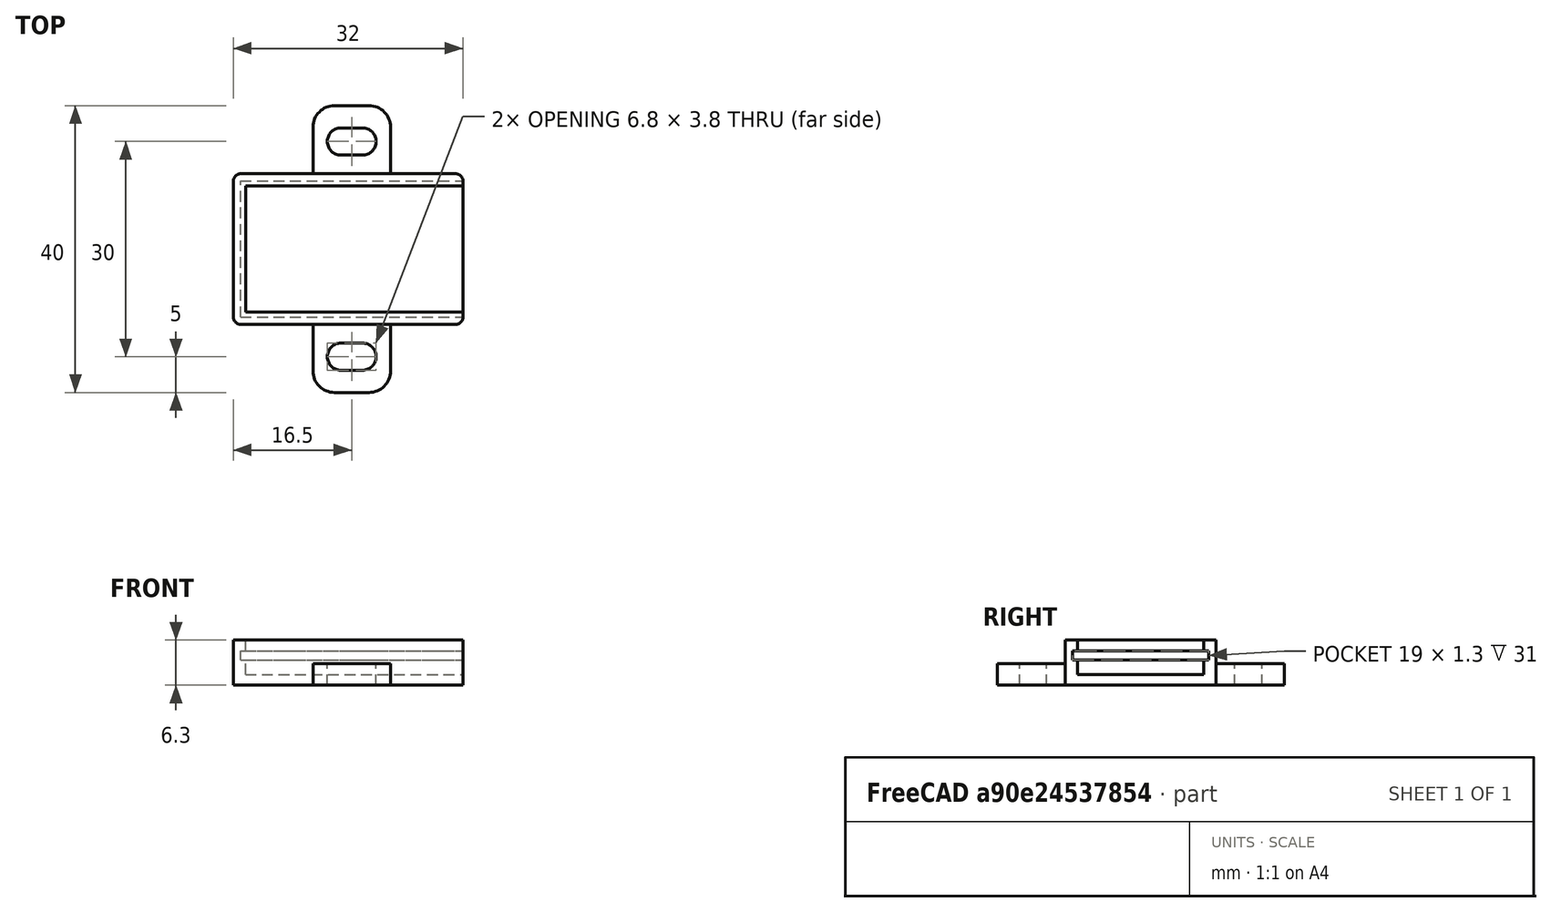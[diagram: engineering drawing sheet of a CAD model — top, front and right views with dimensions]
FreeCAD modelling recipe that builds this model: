
FCSTD DOCUMENT  (FreeCAD 0.18.4R)
Label: stm8s003f
License: FreeArt
LicenseURL: http://artlibre.org/licence/lal
objects: Part::Box×3, Part::MultiFuse×2, Spreadsheet::Sheet×1, Part::Fillet×1, Part::Feature×1, Part::Cut×1, App::Part×1
note: 8 computed .brp shape members not serialized (recipe doc carries the construction recipe); baked Part::Feature solids carry a one-line shape summary decoded from their .brp

FEATURE [Spreadsheet::Sheet] Spreadsheet  label="p"
  cells = A1=pcb_x; B1(pcb_x)=31; A2=pcb_y; B2(pcb_y)=19; A3=pcb_z; B3(pcb_z)=1.3; A4=pcb_under; B4(pcb_under)=2; A5=side_wall; B5(side_wall)=1; A6=pcb_side_lane; B6(pcb_side_lane)=0.7; A7=bottom_wall; B7(bottom_wall)=1.5; A8=pcb_above; B8(pcb_above)=1.5
FEATURE [Part::Box] Box  label="external cube"
  AttacherType = Attacher::AttachEngine3D
  Height = 6.3
  Length = 32
  Width = 21
  expr: Height = p.bottom_wall + p.pcb_under + p.pcb_z + p.pcb_above
  expr: Width = p.pcb_y + 2 * p.side_wall
  expr: Length = p.pcb_x + p.side_wall
FEATURE [Part::Box] Box006  label="internal cube"
  AttacherType = Attacher::AttachEngine3D
  Height = 4.8
  Length = 30.6
  Placement = pos=(1.7,1.7,1.5) rot=(0,0,1;0rad)
  Width = 17.6
  expr: Placement.Base.y = p.side_wall + p.pcb_side_lane
  expr: Placement.Base.x = p.side_wall + p.pcb_side_lane
  expr: Placement.Base.z = p.bottom_wall
  expr: Height = p.pcb_under + p.pcb_z + p.pcb_above
  expr: Width = p.pcb_y - 2 * p.pcb_side_lane
  expr: Length = p.pcb_x - 2 * p.pcb_side_lane + p.side_wall
FEATURE [Part::Box] Box007  label="pcb extract cube"
  AttacherType = Attacher::AttachEngine3D
  Height = 1.3
  Length = 31
  Placement = pos=(1,1,3.5) rot=(0,0,1;0rad)
  Width = 19
  expr: Placement.Base.y = p.side_wall
  expr: Placement.Base.x = p.side_wall
  expr: Length = p.pcb_x
  expr: Width = p.pcb_y
  expr: Placement.Base.z = p.bottom_wall + p.pcb_under
  expr: Height = p.pcb_z
FEATURE [Part::MultiFuse] Fusion  label="extract fusion"
  Shapes = -> [Box006,Box007]
FEATURE [Part::Fillet] Fillet  label="external fillet"
  Base = -> Box
  Edges = 4 edges r=1: [Edge1,Edge3,Edge5,Edge7]
FEATURE [Part::Feature] Cut002001  label="attach plane y dir001"
  shape: bbox 10.8 x 40 x 3 mm, 18 faces (baked)
FEATURE [Part::MultiFuse] Fusion001  label="stm8 fusion"
  Shapes = -> [Fillet,Cut002001]
FEATURE [Part::Cut] Cut  label="stm8 cut"
  Base = -> Fusion001
  Tool = -> Fusion
FEATURE [App::Part] Part  label="stm8 pcb box part"
  Group = -> [Box,Fillet,Fusion001,Fusion,Box007,Box006,Cut]
  Origin = -> Origin
